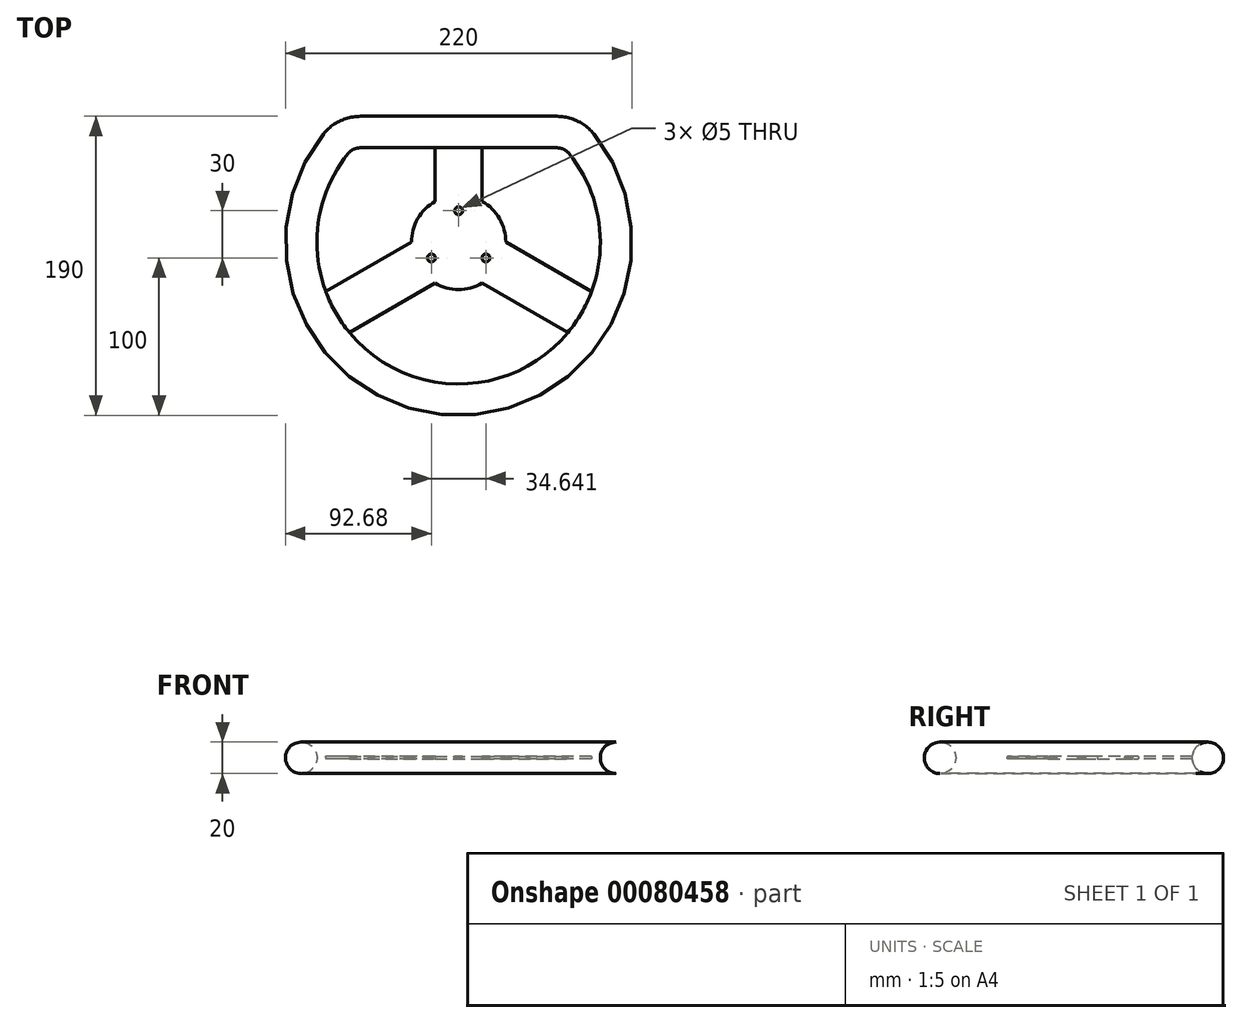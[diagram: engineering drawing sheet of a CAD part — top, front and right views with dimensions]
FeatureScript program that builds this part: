
annotation { "Feature Type Name" : "Feature", "Feature Type Description" : "" }
export const myFeature = defineFeature(function(context is Context, id is Id, definition is map)
    precondition{}
    {
        {
            var Q0;
            Q0=qCreatedBy(makeId("Top.planeOp"),FACE);
            var sketch = newSketch(context, id + "F0", { "sketchPlane" : qUnion([Q0])});
            skCircle(sketch, "E0", {"center": v(0, 0) * mm, "radius": 100 * mm, "construction": true});
            skLineSegment(sketch, "E1", {"start": v(-71.41, 70) * mm, "end": v(71.41, 70) * mm, "construction": true});
            skCircle(sketch, "E2", {"center": v(0, 0) * mm, "radius": 30 * mm});
            skLineSegment(sketch, "E3", {"start": v(-15, 70) * mm, "end": v(-15, 25.98) * mm});
            skLineSegment(sketch, "E4", {"start": v(15, 70) * mm, "end": v(15, 25.98) * mm});
            skLineSegment(sketch, "E5", {"start": v(-15, 70) * mm, "end": v(15, 70) * mm});
            skLineSegment(sketch, "E6", {"start": v(-30, 0) * mm, "end": v(-93.12, -36.44) * mm});
            skLineSegment(sketch, "E7", {"start": v(-93.12, -36.44) * mm, "end": v(-78.12, -62.42) * mm});
            skLineSegment(sketch, "E8", {"start": v(-78.12, -62.42) * mm, "end": v(-15, -25.98) * mm});
            skLineSegment(sketch, "E9", {"start": v(15, -25.98) * mm, "end": v(78.12, -62.42) * mm});
            skLineSegment(sketch, "E10", {"start": v(78.12, -62.42) * mm, "end": v(93.12, -36.44) * mm});
            skLineSegment(sketch, "E11", {"start": v(93.12, -36.44) * mm, "end": v(30, 0) * mm});
            skSolve(sketch);
        }
        {
            var Q0;
            Q0 = qSketchRegion(id + "F0", true);
            extrude(context, id + "F1", {"entities" : qUnion([Q0]), "depth" : 1.6 * mm, "symmetric" : true});
        }
        {
            var Q0;
            Q0=makeQuery(id+"F1.opExtrude","CAP_FACE",FACE,{"disambiguationData":[OSD([sQuery(id+"F0.wireOp",EDGE,"E2"),sQuery(id+"F0.wireOp",EDGE,"E3"),sQuery(id+"F0.wireOp",EDGE,"E4"),sQuery(id+"F0.wireOp",EDGE,"E5"),sQuery(id+"F0.wireOp",EDGE,"E6"),sQuery(id+"F0.wireOp",EDGE,"E7"),sQuery(id+"F0.wireOp",EDGE,"E8"),sQuery(id+"F0.wireOp",EDGE,"E9"),sQuery(id+"F0.wireOp",EDGE,"E10"),sQuery(id+"F0.wireOp",EDGE,"E11")])],"isStart":false});
            var sketch = newSketch(context, id + "F2", { "sketchPlane" : qUnion([Q0])});
            skCircle(sketch, "E12", {"center": v(0, 0) * mm, "radius": 20 * mm, "construction": true});
            skCircle(sketch, "E13", {"center": v(0, 20) * mm, "radius": 2.5 * mm});
            skCircle(sketch, "E14.1.0", {"center": v(-17.32, -10) * mm, "radius": 2.5 * mm});
            skCircle(sketch, "E14.2.0", {"center": v(17.32, -10) * mm, "radius": 2.5 * mm});
            skSolve(sketch);
        }
        {
            var Q0;
            Q0 = qSketchRegion(id + "F2", true);
            extrude(context, id + "F3", {"entities" : qUnion([Q0]), "operationType" : NewBodyOperationType.REMOVE, "endBound" : BoundingType.THROUGH_ALL, "oppositeDirection" : true, "depth" : 25 * mm});
        }
        {
            var Q0;
            Q0=qCreatedBy(makeId("Top.planeOp"),FACE);
            var sketch = newSketch(context, id + "F4", { "sketchPlane" : qUnion([Q0])});
            skLineSegment(sketch, "E15.0", {"start": v(0, 70) * mm, "end": v(62.45, 70) * mm});
            skArc(sketch, "E15.1", {"start": v(0, -100) * mm, "mid": v(90.14, -43.3) * mm, "end": v(78.06, 62.5) * mm});
            skLineSegment(sketch, "E16", {"start": v(0, 100) * mm, "end": v(0, -100) * mm, "construction": true});
            skPoint(sketch, "E17.orphan", {"position": v(-71.41, 70) * mm});
            skPoint(sketch, "E18.visualSharp", {"position": v(71.41, 70) * mm});
            skArc(sketch, "E18.filletArc", {"start": v(78.06, 62.5) * mm, "mid": v(71.11, 68.03) * mm, "end": v(62.45, 70) * mm});
            skSolve(sketch);
        }
        {
            var Q0;
            Q0=qCreatedBy(makeId("Right.planeOp"),FACE);
            var sketch = newSketch(context, id + "F5", { "sketchPlane" : qUnion([Q0])});
            skPoint(sketch, "E19.0", {"position": v(70, 0) * mm});
            skCircle(sketch, "E20", {"center": v(70, 0) * mm, "radius": 10 * mm});
            skSolve(sketch);
        }
        {
            var Q0;
            Q0=makeQuery(id+"F5.imprint","IMPRINT",FACE,{"disambiguationData":[TD([[makeQuery(id+"F5.imprint","IMPRINT",EDGE,{"derivedFrom":sQuery(id+"F5.wireOp",EDGE,"E20")}),1.0]])]});
            var Q1;
            Q1 = qConstructionFilter(qBodyType(qCreatedBy(id + "F4" ,EDGE), BodyType.WIRE), ConstructionObject.NO);
            sweep(context, id + "F6", {"profiles" : qUnion([Q0]), "path" : qUnion([Q1])});
        }
        {
            var Q0;
            Q0=makeQuery(id+"F6.opSweep","SWEPT_BODY",BODY,{"disambiguationData":[OSD([sQuery(id+"F4.wireOp",EDGE,"E15.0"),sQuery(id+"F5.wireOp",EDGE,"E20")])]});
            var Q1;
            Q1=qCreatedBy(makeId("Right.planeOp"),FACE);
            mirror(context, id + "F7", {"operationType" : NewBodyOperationType.ADD, "entities" : qUnion([Q0]), "mirrorPlane" : qUnion([Q1])});
        }
    });
